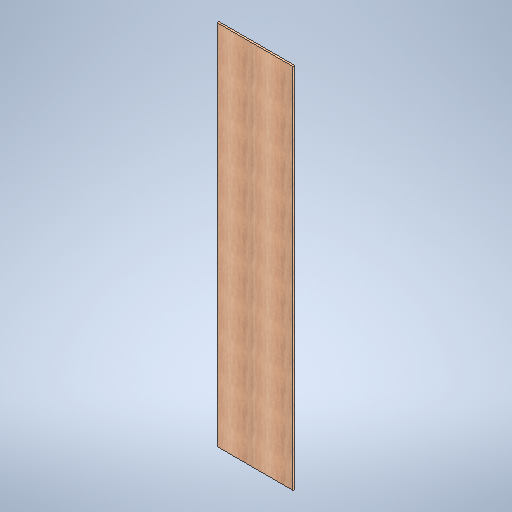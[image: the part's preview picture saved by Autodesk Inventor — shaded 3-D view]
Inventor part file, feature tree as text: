
AUTODESK INVENTOR PART (.ipt)
format: ipt  version: 2025.1 (Build 291241020, 241B)  size: 337,408 bytes
history: native  units: in
note: dims shown in document units (in); Inventor stores cm internally (conversion verified against a paired STEP export)
features: extrude x1, sketch x1
ambient origin geometry x8: Origin, YZ Plane, XZ Plane, XY Plane, X Axis, Y Axis, Z Axis, Center Point
bodies: Solid1 (feature_tree)
feature tree (2):
  extrude  "Extrusion1"  Depth=19.831in
  sketch  "Sketch1"  dims[d2=96.0in d3=19.831in d4=0.5in d5=0.0in]
